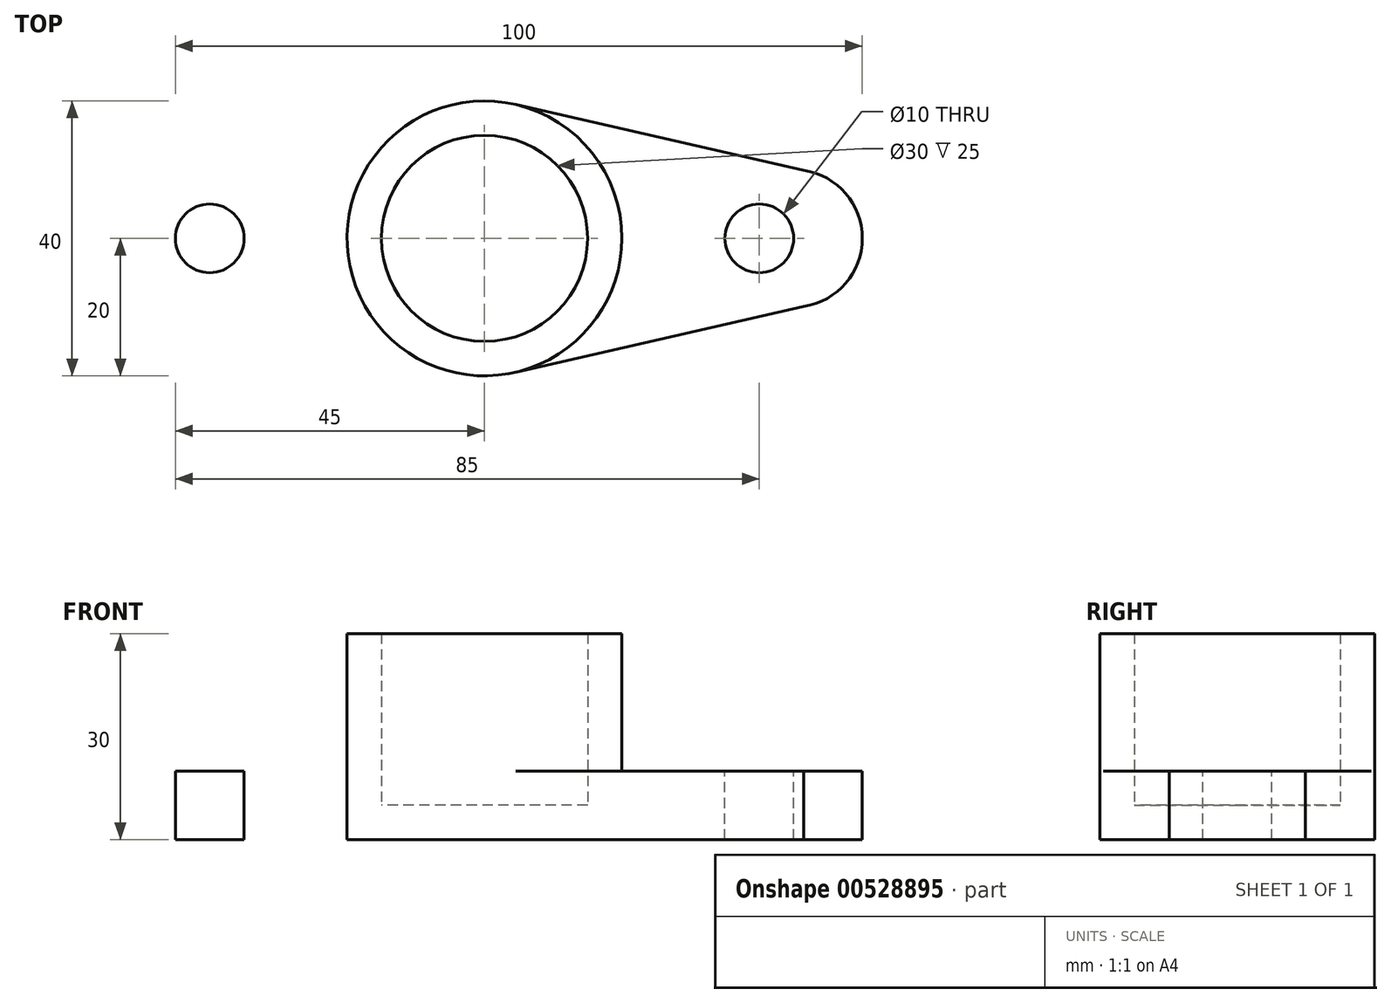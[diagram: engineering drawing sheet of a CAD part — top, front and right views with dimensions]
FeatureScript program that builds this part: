
annotation { "Feature Type Name" : "Feature", "Feature Type Description" : "" }
export const myFeature = defineFeature(function(context is Context, id is Id, definition is map)
    precondition{}
    {
        {
            var Q0;
            Q0=qCreatedBy(makeId("Top.planeOp"),FACE);
            var sketch = newSketch(context, id + "F0", { "sketchPlane" : qUnion([Q0])});
            skArc(sketch, "E0", {"start": v(46.47, -9.9) * mm, "mid": v(55, 0) * mm, "end": v(46.47, 9.9) * mm});
            skArc(sketch, "E1", {"start": v(-4.56, -19.47) * mm, "mid": v(0, -20) * mm, "end": v(4.56, -19.47) * mm});
            skLineSegment(sketch, "E2", {"start": v(0, 49.03) * mm, "end": v(0, -52.2) * mm, "construction": true});
            skArc(sketch, "E3.MirrorC", {"start": v(-46.47, -9.9) * mm, "mid": v(-55, 0) * mm, "end": v(-46.47, 9.9) * mm});
            skLineSegment(sketch, "E4", {"start": v(-4.56, 19.47) * mm, "end": v(-47.97, 9.55) * mm});
            skLineSegment(sketch, "E5", {"start": v(-61.62, 0) * mm, "end": v(55.67, 0) * mm, "construction": true});
            skLineSegment(sketch, "E6.MirrorCS", {"start": v(4.56, 19.47) * mm, "end": v(47.97, 9.55) * mm});
            skLineSegment(sketch, "E7.MirrorCS", {"start": v(-4.56, -19.47) * mm, "end": v(-47.97, -9.55) * mm});
            skLineSegment(sketch, "E8.MirrorCS", {"start": v(4.56, -19.47) * mm, "end": v(47.97, -9.55) * mm});
            skArc(sketch, "E9.trimOffspring", {"start": v(4.56, 19.47) * mm, "mid": v(0, 20) * mm, "end": v(-4.56, 19.47) * mm});
            skSolve(sketch);
        }
        {
            var Q0;
            Q0 = qSketchRegion(id + "F0", true);
            extrude(context, id + "F1", {"entities" : qUnion([Q0]), "depth" : 10 * mm, "offsetDistance" : 25 * mm});
        }
        {
            var Q0;
            Q0=makeQuery(id+"F1.opExtrude","CAP_FACE",FACE,{"disambiguationData":[OSD([sQuery(id+"F0.wireOp",EDGE,"E0"),sQuery(id+"F0.wireOp",EDGE,"E1"),sQuery(id+"F0.wireOp",EDGE,"E3.MirrorC"),sQuery(id+"F0.wireOp",EDGE,"E4"),sQuery(id+"F0.wireOp",EDGE,"E6.MirrorCS"),sQuery(id+"F0.wireOp",EDGE,"E7.MirrorCS"),sQuery(id+"F0.wireOp",EDGE,"E8.MirrorCS"),sQuery(id+"F0.wireOp",EDGE,"E9.trimOffspring")])],"isStart":false});
            var sketch = newSketch(context, id + "F2", { "sketchPlane" : qUnion([Q0])});
            skLineSegment(sketch, "E10", {"start": v(0, 57.56) * mm, "end": v(0, -55.5) * mm, "construction": true});
            skLineSegment(sketch, "E11", {"start": v(0, 0) * mm, "end": v(40, 0) * mm, "construction": true});
            skCircle(sketch, "E12", {"center": v(40, 0) * mm, "radius": 5 * mm});
            skCircle(sketch, "E13.MirrorC", {"center": v(-40, 0) * mm, "radius": 5 * mm});
            skCircle(sketch, "E14", {"center": v(0, 0) * mm, "radius": 20 * mm});
            skCircle(sketch, "E15", {"center": v(0, 0) * mm, "radius": 15 * mm});
            skSolve(sketch);
        }
        {
            var Q0;
            Q0=makeQuery(id+"F2.imprint","IMPRINT",FACE,{"disambiguationData":[TD([[makeQuery(id+"F2.imprint","IMPRINT",EDGE,{"derivedFrom":sQuery(id+"F2.wireOp",EDGE,"E13.MirrorC")}),-1.0]])]});
            var Q1;
            Q1=makeQuery(id+"F2.imprint","IMPRINT",FACE,{"disambiguationData":[TD([[makeQuery(id+"F2.imprint","IMPRINT",EDGE,{"derivedFrom":sQuery(id+"F2.wireOp",EDGE,"E12")}),1.0]])]});
            extrude(context, id + "F3", {"entities" : qUnion([Q0, Q1]), "operationType" : NewBodyOperationType.REMOVE, "endBound" : BoundingType.THROUGH_ALL, "oppositeDirection" : true, "depth" : 25 * mm, "offsetDistance" : 25 * mm});
        }
        {
            var Q0;
            {var subQ0=sQuery(id+"F2.wireOp",EDGE,"E14");var subQ1=makeQuery(id+"F2.imprint","INTERSECT",VERTEX,{"derivedFrom":[makeQuery(id+"F1.opExtrude","CAP_EDGE",EDGE,{"disambiguationData":[OSD([sQuery(id+"F0.wireOp",EDGE,"E4")])],"isStart":false}),subQ0]});Q0=makeQuery(id+"F2.imprint","IMPRINT",FACE,{"disambiguationData":[TD([[makeQuery(id+"F2.imprint","IMPRINT",EDGE,{"disambiguationData":[TD([[subQ1,1.0]])],"derivedFrom":subQ0}),1.0]])]});}
            extrude(context, id + "F4", {"entities" : qUnion([Q0]), "operationType" : NewBodyOperationType.ADD, "depth" : 20 * mm, "offsetDistance" : 25 * mm});
        }
        {
            var Q0;
            Q0=makeQuery(id+"F4.boolean.opBoolean","SPLIT",FACE,{"disambiguationData":[TD([makeQuery(id+"F4.opExtrude","SWEPT_FACE",FACE,{"disambiguationData":[OSD([sQuery(id+"F2.wireOp",EDGE,"E15")])]})])],"derivedFrom":makeQuery(id+"F1.opExtrude","CAP_FACE",FACE,{"disambiguationData":[OSD([sQuery(id+"F0.wireOp",EDGE,"E0"),sQuery(id+"F0.wireOp",EDGE,"E1"),sQuery(id+"F0.wireOp",EDGE,"E3.MirrorC"),sQuery(id+"F0.wireOp",EDGE,"E4"),sQuery(id+"F0.wireOp",EDGE,"E6.MirrorCS"),sQuery(id+"F0.wireOp",EDGE,"E7.MirrorCS"),sQuery(id+"F0.wireOp",EDGE,"E8.MirrorCS"),sQuery(id+"F0.wireOp",EDGE,"E9.trimOffspring")])],"isStart":false})});
            extrude(context, id + "F5", {"entities" : qUnion([Q0]), "operationType" : NewBodyOperationType.REMOVE, "endBound" : BoundingType.SYMMETRIC, "oppositeDirection" : true, "depth" : 10 * mm, "offsetDistance" : 25 * mm});
        }
    });
